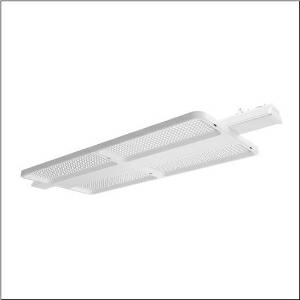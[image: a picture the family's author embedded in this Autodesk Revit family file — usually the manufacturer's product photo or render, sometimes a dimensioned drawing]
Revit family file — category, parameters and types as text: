
# Revit family: highbay_11_fur_licross_tragschiene_maxi_51hn12db4qla
name_source: partatom
category: Lighting Fixtures
units: mm (PartAtom-declared; Revit-internal decimal feet)

## family parameters
Cut with Voids When Loaded = No
Host = Face
Light Source = No
Part Type = Normal
Room Calculation Point = No
Round Connector Dimension = Use Diameter
Shared = No

## types (1)
- --- (1 x LED, 36000 lm, 177.7 W, 4000K)
    Apparent Load = 178 VA
    CIE Flux Codes = 87 98 100 100 100
    Color Rendering = 80
    Color Temperature = 4000K
    Default Elevation = 1800 mm
    Description = high bay luminaire Highbay 11 for Licross trunking rail maxi; direct symmetric wide distribution, light control with lens of PMMA; UGR ≤ 22 (X = 4H | Y = 8H | S = 0.25H | reflection values 70/50/20); luminous flux: 36.000lm; light colour: 840, colour temperature: 4000K, MacAdam ≤ 2 SDCM (initial), colour rendering: CRI > 80; luminous efficacy: 202,6lm/W; rated service life: 100.000h (L95) at AT= 25°C; control: DALI 2; luminaire connection: plug, 5-pole, with phase selectionmains connection: 230..240V, AC 50/60Hz; connected load: 177,7W; protection rating (complete): IP64; insulation class (complete): insulation class I (protective earthing); protection symbol: D; impact resistance: IK06; certification: CE, ENEC, VDE, UKCA; internal wiring halogen-free; luminaire LABS conformity tested according to VDMA 24364:2018-05; Suitable for use in the food industry according to the specifications of IFS-Food, HACCP and/or BRC; housing frame of high-performance plastic PA6, matt traffic white (RAL 9016); cover of PMMA; fixing on rail side of steel, galvanised, white; blank cover of PC/ABS, traffic white (RAL 9016); dimension (LxWxH): 1.250 x 442 x 71mm; permissible operating ambient temperature: -40..+55°C (reducing of maximum allowable ambient temperature of 5°C with ceiling mounting); packaging unit: 1 piece
    Height = 72 mm  [stored 0.23622 ft]
    Lamp = 1 x LED
    Lamp Light Flux = 36000 lm
    Lamp Power = 177.7 W
    Lamp count = 1
    Length = 946 mm
    Luminous efficacy = 203 lm/W
    Manufacturer = Siteco
    ModVariant = No
    Model = 51HN12DB4QLA
    Mounting Place = Ceiling
    Mounting Type = Pendant
    Number of Poles = 1
    OnlyDefault = Yes
    Power Factor = 1
    Product Name = Highbay 11 für Licross Tragschiene maxi
    Product group = high bay luminaire
    ProductGroupID = 902
    Protection Class = Protection class I
    Protection Degree = IP 64
    RLX_Detail_Level = 1
    RLX_Emergency_Light_Flux = 0 lm
    RLX_Emergency_Type = 0
    RLX_Emergency_Type_DB = No
    RlxData = <blob elided: 24257 chars, md5=190afe41>
    Socket = socket
    Standby Power = 0 W
    System Light Flux = 36000 lm
    System Power = 178 W
    Type Comments = factory setting: luminous flux: 100 % | dim-lin: 254 | 824 mA
    Type Image = l_1361711.jpg
    URL = http://relux.com
    VarID = @adj_027161
    Voltage = 0 V
    Weight = 0.00 kg
    Width = 442 mm

note: [stored X ft] marks values corroborated as IEEE doubles in the binary element streams (Revit-internal decimal feet)

## geometry (parser evidence)
native form markers: Blend x4, Sweep x8
no freeform markers — native parametric forms only
